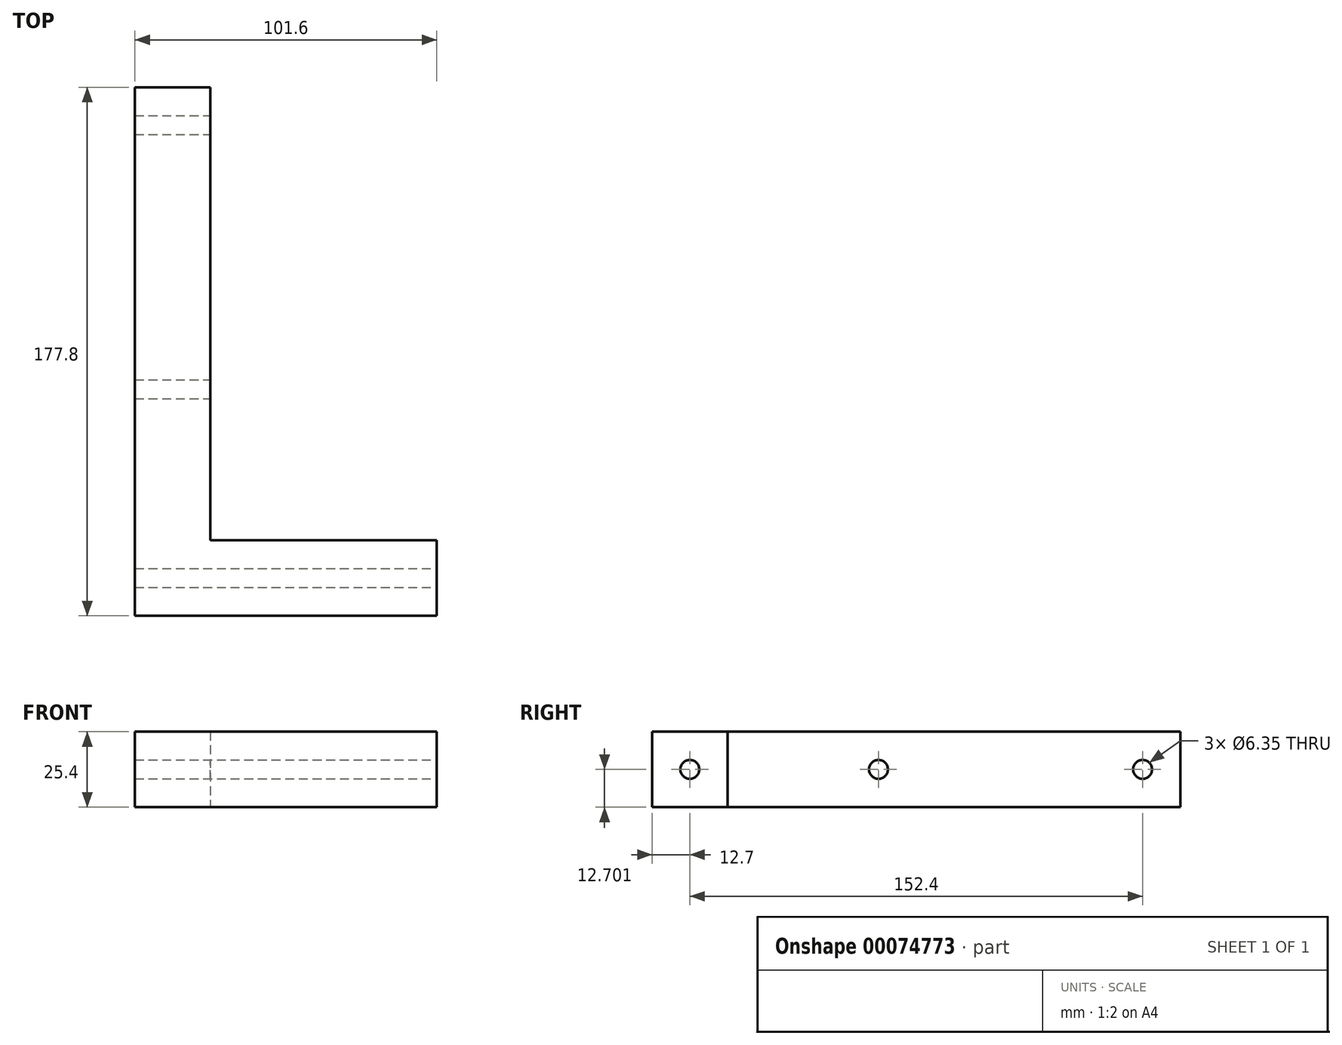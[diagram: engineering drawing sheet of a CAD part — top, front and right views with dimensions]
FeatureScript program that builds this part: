
annotation { "Feature Type Name" : "Feature", "Feature Type Description" : "" }
export const myFeature = defineFeature(function(context is Context, id is Id, definition is map)
    precondition{}
    {
        {
            var Q0;
            Q0=qCreatedBy(makeId("Front.planeOp"),FACE);
            var sketch = newSketch(context, id + "F0", { "sketchPlane" : qUnion([Q0])});
            skLineSegment(sketch, "E0", {"start": v(-36.07, 42.76) * mm, "end": v(-36.07, 17.36) * mm});
            skLineSegment(sketch, "E1", {"start": v(-36.07, 17.36) * mm, "end": v(-10.67, 17.36) * mm});
            skLineSegment(sketch, "E2", {"start": v(-10.67, 17.36) * mm, "end": v(-10.67, 42.76) * mm});
            skLineSegment(sketch, "E3", {"start": v(-10.67, 42.76) * mm, "end": v(-36.07, 42.76) * mm});
            skSolve(sketch);
        }
        {
            var Q0;
            Q0=makeQuery(id+"F0.imprint","IMPRINT",FACE,{"disambiguationData":[TD([[makeQuery(id+"F0.imprint","IMPRINT",EDGE,{"derivedFrom":sQuery(id+"F0.wireOp",EDGE,"E0")}),1.0]])]});
            extrude(context, id + "F1", {"entities" : qUnion([Q0]), "oppositeDirection" : true, "depth" : 177.8 * mm});
        }
        {
            var Q0;
            Q0=makeQuery(id+"F1.opExtrude","SWEPT_FACE",FACE,{"disambiguationData":[OSD([sQuery(id+"F0.wireOp",EDGE,"E2")])]});
            var sketch = newSketch(context, id + "F2", { "sketchPlane" : qUnion([Q0])});
            skPoint(sketch, "E4", {"position": v(12.7, 30.06) * mm});
            skPoint(sketch, "E4.positionSnap0", {"position": v(0, 30.06) * mm});
            skPoint(sketch, "E5", {"position": v(165.1, 30.06) * mm});
            skPoint(sketch, "E5.positionSnap0", {"position": v(177.8, 30.06) * mm});
            skSolve(sketch);
        }
        {
            var Q0;
            Q0=sQuery(id+"F2.wireOp",VERTEX,"E4");
            var Q1;
            Q1=sQuery(id+"F2.wireOp",VERTEX,"E5");
            var Q2;
            Q2=makeQuery(id+"F1.opExtrude","SWEPT_BODY",BODY,{"disambiguationData":[OSD([sQuery(id+"F0.wireOp",EDGE,"E0"),sQuery(id+"F0.wireOp",EDGE,"E1"),sQuery(id+"F0.wireOp",EDGE,"E2"),sQuery(id+"F0.wireOp",EDGE,"E3")])]});
            hole(context, id + "F3", {"style" : HoleStyle.SIMPLE, "holeDiameter" : 6.35 * mm, "endStyle" : HoleEndStyle.THROUGH, "locations" : qUnion([Q0, Q1]), "scope" : qUnion([Q2])});
        }
        {
            var Q0;
            Q0=makeQuery(id+"F1.opExtrude","SWEPT_FACE",FACE,{"disambiguationData":[OSD([sQuery(id+"F0.wireOp",EDGE,"E2")])]});
            var sketch = newSketch(context, id + "F4", { "sketchPlane" : qUnion([Q0])});
            skLineSegment(sketch, "E6.bottom", {"start": v(0, 42.76) * mm, "end": v(25.4, 42.76) * mm});
            skLineSegment(sketch, "E6.top", {"start": v(0, 17.36) * mm, "end": v(25.4, 17.36) * mm});
            skLineSegment(sketch, "E6.left", {"start": v(0, 42.76) * mm, "end": v(0, 17.36) * mm});
            skLineSegment(sketch, "E6.right", {"start": v(25.4, 42.76) * mm, "end": v(25.4, 17.36) * mm});
            skSolve(sketch);
        }
        {
            var Q0;
            Q0=makeQuery(id+"F4.imprint","IMPRINT",FACE,{"disambiguationData":[TD([[makeQuery(id+"F4.imprint","IMPRINT",EDGE,{"derivedFrom":sQuery(id+"F4.wireOp",EDGE,"E6.bottom")}),1.0]])]});
            extrude(context, id + "F5", {"entities" : qUnion([Q0]), "operationType" : NewBodyOperationType.ADD, "depth" : 76.2 * mm});
        }
        {
            var Q0;
            Q0=makeQuery(id+"F1.opExtrude","SWEPT_FACE",FACE,{"disambiguationData":[OSD([sQuery(id+"F0.wireOp",EDGE,"E2")])]});
            var sketch = newSketch(context, id + "F6", { "sketchPlane" : qUnion([Q0])});
            skPoint(sketch, "E7", {"position": v(76.2, 30.06) * mm});
            skPoint(sketch, "E7.positionSnap0", {"position": v(177.8, 30.06) * mm});
            skSolve(sketch);
        }
        {
            var Q0;
            Q0=sQuery(id+"F6.wireOp",VERTEX,"E7");
            var Q1;
            Q1=makeQuery(id+"F1.opExtrude","SWEPT_BODY",BODY,{"disambiguationData":[OSD([sQuery(id+"F0.wireOp",EDGE,"E0"),sQuery(id+"F0.wireOp",EDGE,"E1"),sQuery(id+"F0.wireOp",EDGE,"E2"),sQuery(id+"F0.wireOp",EDGE,"E3")])]});
            hole(context, id + "F7", {"style" : HoleStyle.SIMPLE, "endStyle" : HoleEndStyle.THROUGH, "holeDiameter" : 6.35 * mm, "locations" : qUnion([Q0]), "scope" : qUnion([Q1]), "isTappedThrough" : true});
        }
    });
